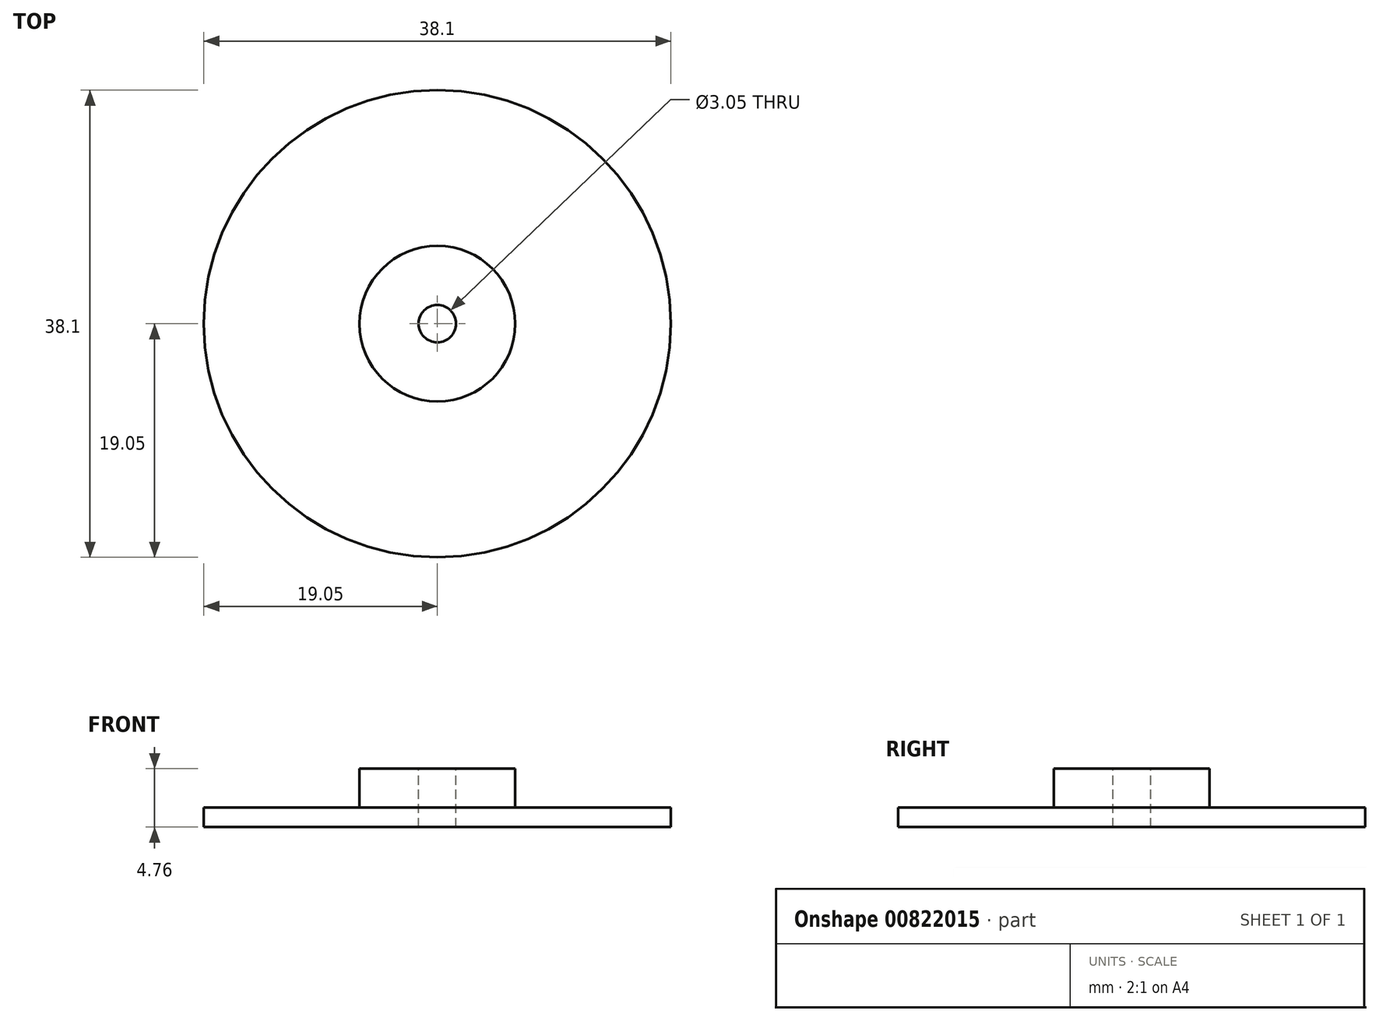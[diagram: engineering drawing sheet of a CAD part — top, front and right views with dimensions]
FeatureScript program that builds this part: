
annotation { "Feature Type Name" : "Feature", "Feature Type Description" : "" }
export const myFeature = defineFeature(function(context is Context, id is Id, definition is map)
    precondition{}
    {
        {
            var Q0;
            Q0=qCreatedBy(makeId("Top.planeOp"),FACE);
            var sketch = newSketch(context, id + "F0", { "sketchPlane" : qUnion([Q0])});
            skCircle(sketch, "E0", {"center": v(0, 0) * mm, "radius": 19.05 * mm});
            skSolve(sketch);
        }
        {
            var Q0;
            Q0=makeQuery(id+"F0.imprint","IMPRINT",FACE,{"disambiguationData":[TD([[makeQuery(id+"F0.imprint","IMPRINT",EDGE,{"derivedFrom":sQuery(id+"F0.wireOp",EDGE,"E0")}),1.0]])]});
            extrude(context, id + "F1", {"entities" : qUnion([Q0]), "depth" : 1.59 * mm, "offsetDistance" : 25.4 * mm});
        }
        {
            var Q0;
            Q0=makeQuery(id+"F1.opExtrude","CAP_FACE",FACE,{"disambiguationData":[OSD([sQuery(id+"F0.wireOp",EDGE,"E0")])],"isStart":false});
            var sketch = newSketch(context, id + "F2", { "sketchPlane" : qUnion([Q0])});
            skCircle(sketch, "E1", {"center": v(0, 0) * mm, "radius": 6.35 * mm});
            skSolve(sketch);
        }
        {
            var Q0;
            Q0=makeQuery(id+"F2.imprint","IMPRINT",FACE,{"disambiguationData":[TD([[makeQuery(id+"F2.imprint","IMPRINT",EDGE,{"derivedFrom":sQuery(id+"F2.wireOp",EDGE,"E1")}),1.0]])]});
            extrude(context, id + "F3", {"entities" : qUnion([Q0]), "operationType" : NewBodyOperationType.ADD, "depth" : 3.17 * mm, "offsetDistance" : 25.4 * mm});
        }
        {
            var Q0;
            Q0=makeQuery(id+"F3.opExtrude","CAP_FACE",FACE,{"disambiguationData":[OSD([sQuery(id+"F2.wireOp",EDGE,"E1")])],"isStart":false});
            var sketch = newSketch(context, id + "F4", { "sketchPlane" : qUnion([Q0])});
            skCircle(sketch, "E2", {"center": v(0, 0) * mm, "radius": 1.52 * mm});
            skSolve(sketch);
        }
        {
            var Q0;
            Q0=makeQuery(id+"F4.imprint","IMPRINT",FACE,{"disambiguationData":[TD([[makeQuery(id+"F4.imprint","IMPRINT",EDGE,{"derivedFrom":sQuery(id+"F4.wireOp",EDGE,"E2")}),1.0]])]});
            var Q1;
            Q1=sQuery(id+"F4.wireOp",EDGE,"E2");
            extrude(context, id + "F5", {"entities" : qUnion([Q0]), "operationType" : NewBodyOperationType.REMOVE, "surfaceEntities" : qUnion([Q1]), "endBound" : BoundingType.THROUGH_ALL, "oppositeDirection" : true, "depth" : 25.4 * mm, "offsetDistance" : 25.4 * mm});
        }
    });
